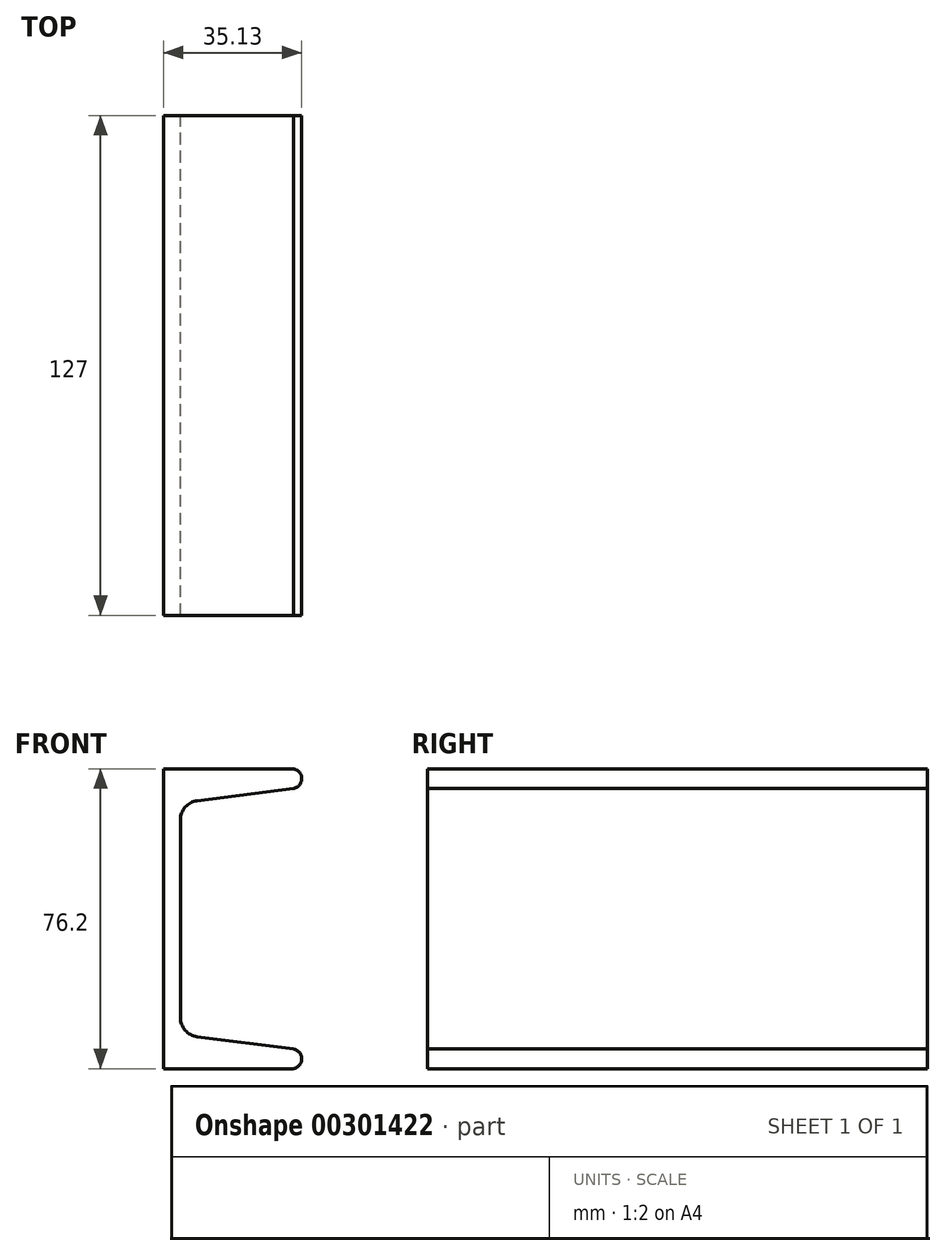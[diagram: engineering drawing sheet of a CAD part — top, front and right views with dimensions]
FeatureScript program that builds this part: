
annotation { "Feature Type Name" : "Feature", "Feature Type Description" : "" }
export const myFeature = defineFeature(function(context is Context, id is Id, definition is map)
    precondition{}
    {
        {
            var Q0;
            Q0=qCreatedBy(makeId("Front.planeOp"),FACE);
            var sketch = newSketch(context, id + "F0", { "sketchPlane" : qUnion([Q0])});
            skLineSegment(sketch, "E0", {"start": v(0, -38.1) * mm, "end": v(33.02, -38.1) * mm});
            skArc(sketch, "E1", {"start": v(33.02, -38.1) * mm, "mid": v(35.13, -35.6) * mm, "end": v(33.02, -33.1) * mm});
            skLineSegment(sketch, "E2", {"start": v(33.02, -33.1) * mm, "end": v(8.56, -29.97) * mm});
            skLineSegment(sketch, "E3", {"start": v(4.32, -25.16) * mm, "end": v(4.32, 0) * mm});
            skLineSegment(sketch, "E4.MirrorCS", {"start": v(4.32, 25.16) * mm, "end": v(4.32, 0) * mm});
            skLineSegment(sketch, "E5.MirrorCS", {"start": v(0, 38.1) * mm, "end": v(33.02, 38.1) * mm});
            skLineSegment(sketch, "E6.MirrorCS", {"start": v(33.02, 33.1) * mm, "end": v(8.56, 29.97) * mm});
            skArc(sketch, "E7.MirrorCS", {"start": v(33.02, 38.1) * mm, "mid": v(35.13, 35.6) * mm, "end": v(33.02, 33.1) * mm});
            skLineSegment(sketch, "E8", {"start": v(0, 38.1) * mm, "end": v(0, -38.1) * mm});
            skPoint(sketch, "E9.visualSharp", {"position": v(4.32, -29.43) * mm});
            skArc(sketch, "E9.filletArc", {"start": v(4.32, -25.16) * mm, "mid": v(5.53, -28.36) * mm, "end": v(8.56, -29.97) * mm});
            skPoint(sketch, "E10.visualSharp", {"position": v(4.32, 29.43) * mm});
            skArc(sketch, "E10.filletArc", {"start": v(8.56, 29.97) * mm, "mid": v(5.53, 28.36) * mm, "end": v(4.32, 25.16) * mm});
            skSolve(sketch);
        }
        {
            var Q0;
            Q0=makeQuery(id+"F0.imprint","IMPRINT",FACE,{"disambiguationData":[TD([[makeQuery(id+"F0.imprint","IMPRINT",EDGE,{"derivedFrom":sQuery(id+"F0.wireOp",EDGE,"E0")}),1.0]])]});
            extrude(context, id + "F1", {"entities" : qUnion([Q0]), "depth" : 127 * mm});
        }
    });
